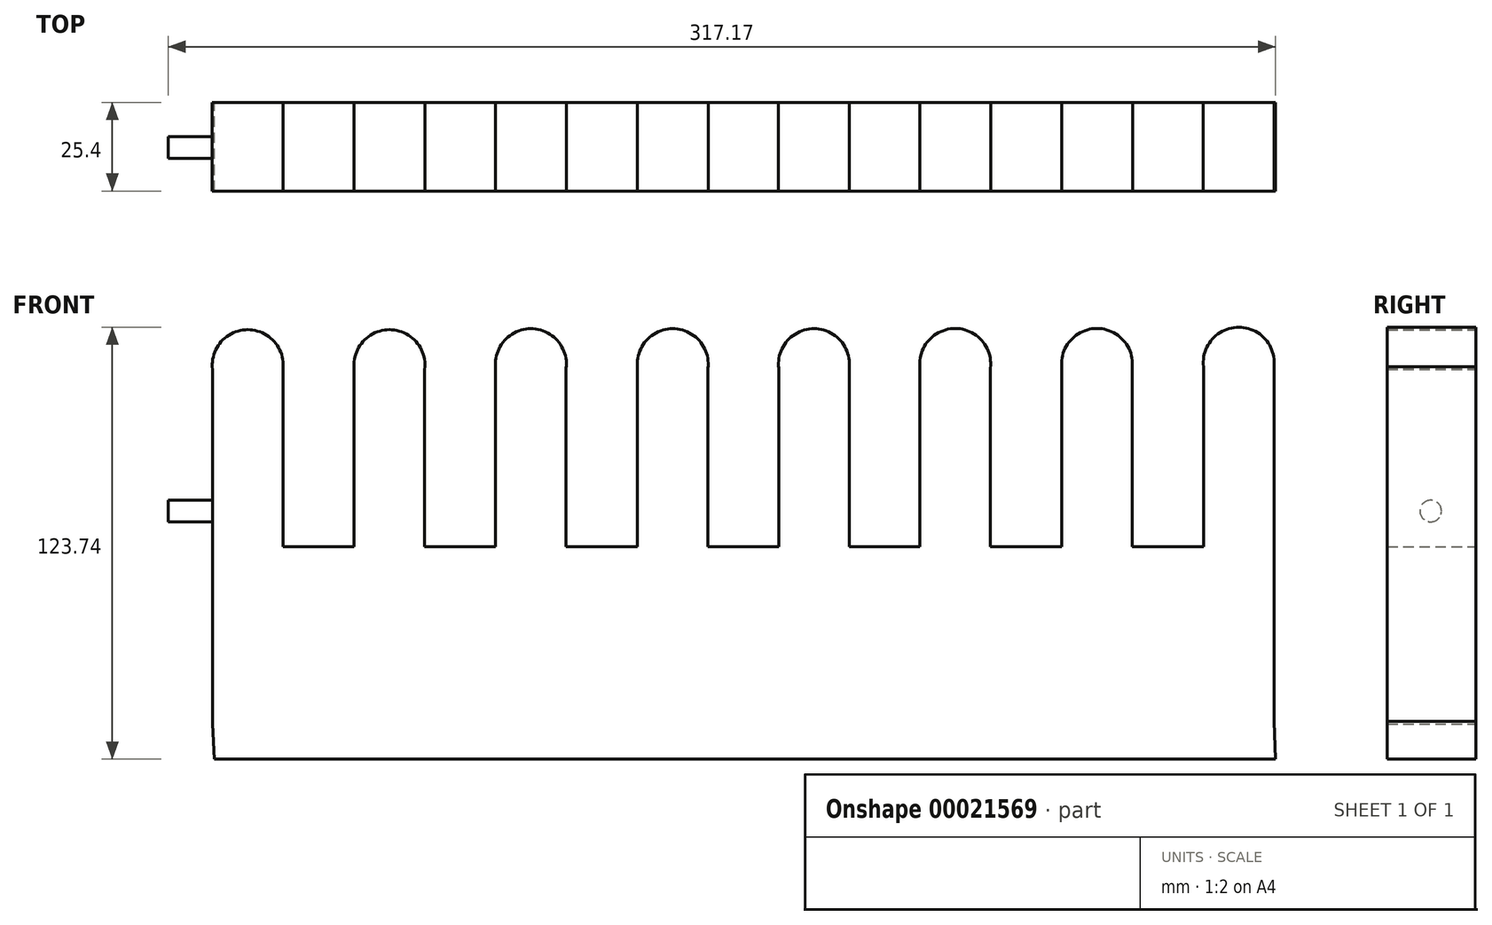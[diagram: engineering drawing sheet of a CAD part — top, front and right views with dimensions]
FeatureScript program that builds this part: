
annotation { "Feature Type Name" : "Feature", "Feature Type Description" : "" }
export const myFeature = defineFeature(function(context is Context, id is Id, definition is map)
    precondition{}
    {
        {
            var Q0;
            Q0=qCreatedBy(makeId("Front.planeOp"),FACE);
            var sketch = newSketch(context, id + "F0", { "sketchPlane" : qUnion([Q0])});
            skCircle(sketch, "E0", {"center": v(-82.84, 64.54) * mm, "radius": 10.16 * mm});
            skLineSegment(sketch, "E1", {"start": v(-72.75, 63.38) * mm, "end": v(-72.75, -38.22) * mm});
            skLineSegment(sketch, "E2", {"start": v(-92.94, 63.38) * mm, "end": v(-92.94, -38.22) * mm});
            skPoint(sketch, "E3.second.point", {"position": v(-52.43, -38.22) * mm});
            skPoint(sketch, "E3.third.point", {"position": v(-55.43, -45.42) * mm});
            skLineSegment(sketch, "E4", {"start": v(-52.31, 63.37) * mm, "end": v(-52.31, -38.23) * mm});
            skCircle(sketch, "E5", {"center": v(-42.22, 64.53) * mm, "radius": 10.16 * mm});
            skLineSegment(sketch, "E6", {"start": v(-32.13, 63.37) * mm, "end": v(-32.13, -38.23) * mm});
            skPoint(sketch, "E7.second.point", {"position": v(-11.8, -38.23) * mm});
            skPoint(sketch, "E7.third.point", {"position": v(-14.8, -45.43) * mm});
            skLineSegment(sketch, "E8", {"start": v(-11.88, 63.37) * mm, "end": v(-11.88, -38.23) * mm});
            skCircle(sketch, "E9", {"center": v(-1.78, 64.53) * mm, "radius": 10.16 * mm});
            skLineSegment(sketch, "E10", {"start": v(8.31, 63.37) * mm, "end": v(8.31, -38.23) * mm});
            skPoint(sketch, "E11.second.point", {"position": v(28.63, -38.23) * mm});
            skPoint(sketch, "E11.third.point", {"position": v(25.64, -45.43) * mm});
            skLineSegment(sketch, "E12", {"start": v(28.59, 63.45) * mm, "end": v(28.59, -38.15) * mm});
            skCircle(sketch, "E13", {"center": v(38.68, 64.6) * mm, "radius": 10.16 * mm});
            skLineSegment(sketch, "E14", {"start": v(48.78, 63.45) * mm, "end": v(48.78, -38.15) * mm});
            skPoint(sketch, "E15.second.point", {"position": v(69.1, -38.15) * mm});
            skPoint(sketch, "E15.third.point", {"position": v(66.1, -45.36) * mm});
            skLineSegment(sketch, "E16", {"start": v(69.18, 63.45) * mm, "end": v(69.18, -38.15) * mm});
            skCircle(sketch, "E17", {"center": v(79.28, 64.6) * mm, "radius": 10.16 * mm});
            skLineSegment(sketch, "E18", {"start": v(89.37, 63.45) * mm, "end": v(89.37, -38.15) * mm});
            skPoint(sketch, "E19.second.point", {"position": v(109.7, -38.15) * mm});
            skPoint(sketch, "E19.third.point", {"position": v(106.7, -45.36) * mm});
            skLineSegment(sketch, "E20", {"start": v(109.78, 63.8) * mm, "end": v(109.78, -37.8) * mm});
            skCircle(sketch, "E21", {"center": v(119.88, 64.96) * mm, "radius": 10.16 * mm});
            skLineSegment(sketch, "E22", {"start": v(129.97, 63.8) * mm, "end": v(129.97, -37.8) * mm});
            skLineSegment(sketch, "E23", {"start": v(-133.45, 63.1) * mm, "end": v(-133.45, -38.5) * mm});
            skCircle(sketch, "E24", {"center": v(-123.36, 64.25) * mm, "radius": 10.16 * mm});
            skLineSegment(sketch, "E25", {"start": v(-113.26, 63.1) * mm, "end": v(-113.26, -38.5) * mm});
            skPoint(sketch, "E26.second.point", {"position": v(-92.94, -38.5) * mm});
            skPoint(sketch, "E26.third.point", {"position": v(-95.94, -45.71) * mm});
            skLineSegment(sketch, "E27", {"start": v(-174.05, 63.1) * mm, "end": v(-174.05, -38.5) * mm});
            skCircle(sketch, "E28", {"center": v(-163.95, 64.25) * mm, "radius": 10.16 * mm});
            skLineSegment(sketch, "E29", {"start": v(-153.86, 63.1) * mm, "end": v(-153.86, -38.5) * mm});
            skPoint(sketch, "E30.second.point", {"position": v(-133.54, -38.5) * mm});
            skPoint(sketch, "E30.third.point", {"position": v(-136.54, -45.71) * mm});
            skLineSegment(sketch, "E31", {"start": v(-144.62, -48.62) * mm, "end": v(130.42, -48.62) * mm});
            skLineSegment(sketch, "E32", {"start": v(-144.62, -48.62) * mm, "end": v(-173.53, -48.62) * mm});
            skLineSegment(sketch, "E33", {"start": v(129.97, -37.8) * mm, "end": v(130.42, -48.62) * mm});
            skLineSegment(sketch, "E34", {"start": v(-174.05, -38.5) * mm, "end": v(-173.53, -48.62) * mm});
            skLineSegment(sketch, "E35", {"start": v(-174.05, 12.3) * mm, "end": v(129.97, 12.3) * mm});
            skSolve(sketch);
        }
        {
            var Q0;
            Q0 = qSketchRegion(id + "F0", true);
            extrude(context, id + "F1", {"entities" : qUnion([Q0]), "depth" : 25.4 * mm});
        }
        {
            var Q0;
            Q0=makeQuery(id+"F1.opExtrude","SWEPT_FACE",FACE,{"disambiguationData":[OSD([sQuery(id+"F0.wireOp",EDGE,"E27")])]});
            var sketch = newSketch(context, id + "F2", { "sketchPlane" : qUnion([Q0])});
            skCircle(sketch, "E36", {"center": v(12.94, 22.45) * mm, "radius": 3.09 * mm});
            skSolve(sketch);
        }
        {
            var Q0;
            Q0 = qSketchRegion(id + "F2", true);
            extrude(context, id + "F3", {"entities" : qUnion([Q0]), "operationType" : NewBodyOperationType.ADD, "depth" : 12.7 * mm});
        }
    });
